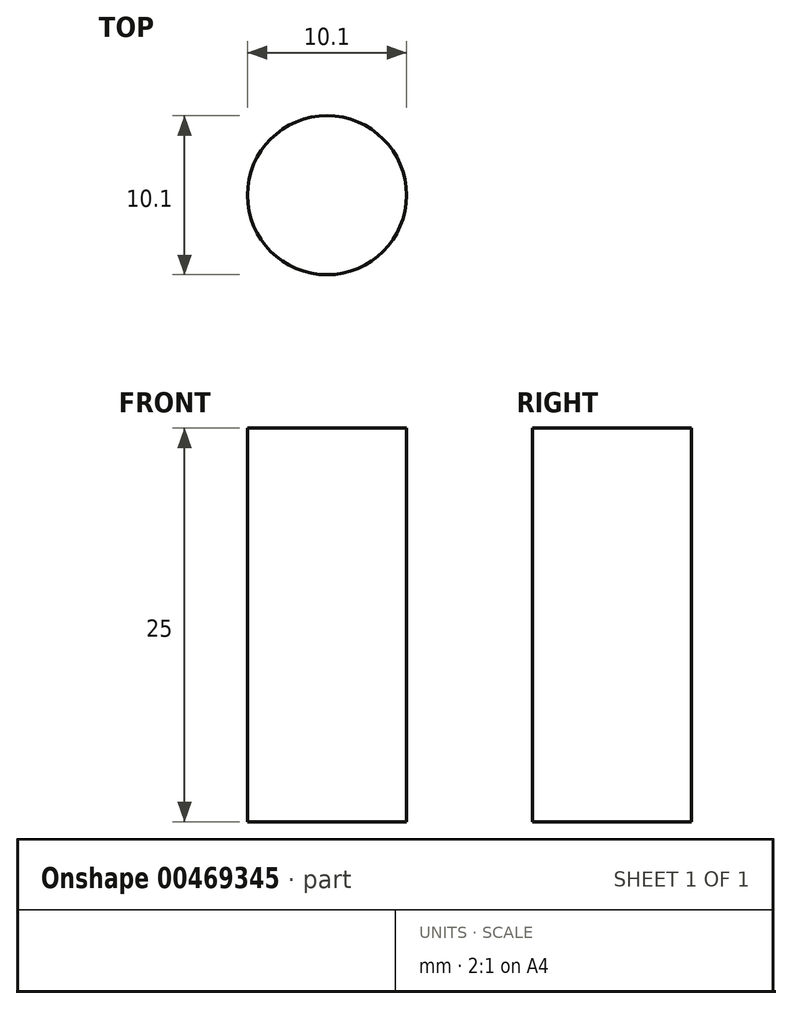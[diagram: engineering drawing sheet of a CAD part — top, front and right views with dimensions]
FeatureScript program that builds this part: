
annotation { "Feature Type Name" : "Feature", "Feature Type Description" : "" }
export const myFeature = defineFeature(function(context is Context, id is Id, definition is map)
    precondition{}
    {
        {
            var Q0;
            Q0=qCreatedBy(makeId("Top.planeOp"),FACE);
            var sketch = newSketch(context, id + "F0", { "sketchPlane" : qUnion([Q0])});
            skLineSegment(sketch, "E0.bottom", {"start": v(0, 0) * mm, "end": v(250, 0) * mm});
            skLineSegment(sketch, "E0.top", {"start": v(0, -80) * mm, "end": v(250, -80) * mm});
            skLineSegment(sketch, "E0.left", {"start": v(0, 0) * mm, "end": v(0, -80) * mm});
            skLineSegment(sketch, "E0.right", {"start": v(250, 0) * mm, "end": v(250, -80) * mm});
            skLineSegment(sketch, "E1.bottom", {"start": v(0, -35) * mm, "end": v(250, -35) * mm});
            skLineSegment(sketch, "E1.top", {"start": v(0, -45) * mm, "end": v(250, -45) * mm});
            skLineSegment(sketch, "E1.left", {"start": v(0, -35) * mm, "end": v(0, -45) * mm});
            skLineSegment(sketch, "E1.right", {"start": v(250, -35) * mm, "end": v(250, -45) * mm});
            skPoint(sketch, "E1.middle", {"position": v(125, -40) * mm});
            skPoint(sketch, "E1.middle.positionSnap0", {"position": v(0, -40) * mm});
            skPoint(sketch, "E1.middle.positionSnap1", {"position": v(125, 0) * mm});
            skPoint(sketch, "E1.centerSnap0", {"position": v(0, -40) * mm});
            skPoint(sketch, "E1.centerSnap1", {"position": v(125, 0) * mm});
            skLineSegment(sketch, "E2.0", {"start": v(-5, 5) * mm, "end": v(-5, -85) * mm});
            skLineSegment(sketch, "E2.1", {"start": v(-5, 5) * mm, "end": v(255, 5) * mm});
            skLineSegment(sketch, "E2.2", {"start": v(255, 5) * mm, "end": v(255, -85) * mm});
            skLineSegment(sketch, "E2.3", {"start": v(-5, -85) * mm, "end": v(255, -85) * mm});
            skLineSegment(sketch, "E3", {"start": v(0, -40) * mm, "end": v(250, -40) * mm});
            skSolve(sketch);
        }
        {
            var Q0;
            Q0=qCreatedBy(makeId("Top.planeOp"),FACE);
            var sketch = newSketch(context, id + "F1", { "sketchPlane" : qUnion([Q0])});
            skLineSegment(sketch, "E4.bottom", {"start": v(0, 0) * mm, "end": v(250, 0) * mm});
            skLineSegment(sketch, "E4.top", {"start": v(0, -140) * mm, "end": v(250, -140) * mm});
            skLineSegment(sketch, "E4.left", {"start": v(0, 0) * mm, "end": v(0, -140) * mm});
            skLineSegment(sketch, "E4.right", {"start": v(250, 0) * mm, "end": v(250, -140) * mm});
            skLineSegment(sketch, "E5.bottom", {"start": v(0, -64) * mm, "end": v(250, -64) * mm});
            skLineSegment(sketch, "E5.top", {"start": v(0, -76) * mm, "end": v(250, -76) * mm});
            skLineSegment(sketch, "E5.left", {"start": v(0, -64) * mm, "end": v(0, -76) * mm});
            skLineSegment(sketch, "E5.right", {"start": v(250, -64) * mm, "end": v(250, -76) * mm});
            skPoint(sketch, "E5.middle", {"position": v(125, -70) * mm});
            skPoint(sketch, "E5.middle.positionSnap0", {"position": v(0, -70) * mm});
            skPoint(sketch, "E5.middle.positionSnap1", {"position": v(125, 0) * mm});
            skPoint(sketch, "E5.centerSnap0", {"position": v(0, -70) * mm});
            skPoint(sketch, "E5.centerSnap1", {"position": v(125, 0) * mm});
            skLineSegment(sketch, "E6.0", {"start": v(-5, 5) * mm, "end": v(-5, -145) * mm});
            skLineSegment(sketch, "E6.1", {"start": v(-5, 5) * mm, "end": v(255, 5) * mm});
            skLineSegment(sketch, "E6.2", {"start": v(255, 5) * mm, "end": v(255, -145) * mm});
            skLineSegment(sketch, "E6.3", {"start": v(-5, -145) * mm, "end": v(255, -145) * mm});
            skLineSegment(sketch, "E7", {"start": v(250, -70) * mm, "end": v(0, -70) * mm});
            skSolve(sketch);
        }
        {
            var Q0;
            Q0=qCreatedBy(makeId("Top.planeOp"),FACE);
            var sketch = newSketch(context, id + "F2", { "sketchPlane" : qUnion([Q0])});
            skLineSegment(sketch, "E8.bottom", {"start": v(0, 0) * mm, "end": v(250, 0) * mm});
            skLineSegment(sketch, "E8.top", {"start": v(0, -225) * mm, "end": v(250, -225) * mm});
            skLineSegment(sketch, "E8.left", {"start": v(0, 0) * mm, "end": v(0, -225) * mm});
            skLineSegment(sketch, "E8.right", {"start": v(250, 0) * mm, "end": v(250, -225) * mm});
            skLineSegment(sketch, "E9.bottom", {"start": v(0, -64) * mm, "end": v(250, -64) * mm});
            skLineSegment(sketch, "E9.top", {"start": v(0, -161) * mm, "end": v(250, -161) * mm});
            skLineSegment(sketch, "E9.left", {"start": v(0, -64) * mm, "end": v(0, -161) * mm});
            skLineSegment(sketch, "E9.right", {"start": v(250, -64) * mm, "end": v(250, -161) * mm});
            skPoint(sketch, "E9.middle", {"position": v(125, -112.5) * mm});
            skPoint(sketch, "E9.middle.positionSnap0", {"position": v(125, 0) * mm});
            skPoint(sketch, "E9.middle.positionSnap1", {"position": v(0, -112.5) * mm});
            skPoint(sketch, "E9.centerSnap0", {"position": v(125, 0) * mm});
            skPoint(sketch, "E9.centerSnap1", {"position": v(0, -112.5) * mm});
            skLineSegment(sketch, "E10.0", {"start": v(-5, 5) * mm, "end": v(-5, -230) * mm});
            skLineSegment(sketch, "E10.1", {"start": v(-5, 5) * mm, "end": v(255, 5) * mm});
            skLineSegment(sketch, "E10.2", {"start": v(255, 5) * mm, "end": v(255, -230) * mm});
            skLineSegment(sketch, "E10.3", {"start": v(-5, -230) * mm, "end": v(255, -230) * mm});
            skLineSegment(sketch, "E11", {"start": v(0, -112.5) * mm, "end": v(250, -112.5) * mm});
            skSolve(sketch);
        }
        {
            var Q0;
            Q0=qCreatedBy(makeId("Top.planeOp"),FACE);
            var sketch = newSketch(context, id + "F3", { "sketchPlane" : qUnion([Q0])});
            skLineSegment(sketch, "E12.0", {"start": v(-20, 20) * mm, "end": v(-20, -245) * mm});
            skLineSegment(sketch, "E12.1", {"start": v(-20, 20) * mm, "end": v(270, 20) * mm});
            skLineSegment(sketch, "E12.2", {"start": v(270, 20) * mm, "end": v(270, -245) * mm});
            skLineSegment(sketch, "E12.3", {"start": v(-20, -245) * mm, "end": v(270, -245) * mm});
            skLineSegment(sketch, "E13.0", {"start": v(20, 20) * mm, "end": v(20, -245) * mm});
            skLineSegment(sketch, "E14", {"start": v(125, 20) * mm, "end": v(125, -245) * mm});
            skLineSegment(sketch, "E15.MirrorCS", {"start": v(230, 20) * mm, "end": v(230, -245) * mm});
            skCircle(sketch, "E16", {"center": v(20, 5) * mm, "radius": 5.05 * mm});
            skCircle(sketch, "E17", {"center": v(-5, -15) * mm, "radius": 5.05 * mm});
            skCircle(sketch, "E18.MirrorC", {"center": v(255, -15) * mm, "radius": 5.05 * mm});
            skCircle(sketch, "E19.MirrorC", {"center": v(230, 5) * mm, "radius": 5.05 * mm});
            skCircle(sketch, "E20.MirrorC", {"center": v(-5, -65) * mm, "radius": 5.05 * mm});
            skCircle(sketch, "E21.MirrorC", {"center": v(20, -85) * mm, "radius": 5.05 * mm});
            skCircle(sketch, "E22.MirrorC", {"center": v(230, -85) * mm, "radius": 5.05 * mm});
            skCircle(sketch, "E23.MirrorC", {"center": v(255, -65) * mm, "radius": 5.05 * mm});
            skCircle(sketch, "E24", {"center": v(-5.05, -40) * mm, "radius": 5.05 * mm});
            skCircle(sketch, "E25.MirrorC", {"center": v(255.05, -40) * mm, "radius": 5.05 * mm});
            skCircle(sketch, "E26.MirrorC", {"center": v(-5, -125) * mm, "radius": 5.05 * mm});
            skCircle(sketch, "E27.MirrorC", {"center": v(20, -145) * mm, "radius": 5.05 * mm});
            skCircle(sketch, "E28.MirrorC", {"center": v(230, -145) * mm, "radius": 5.05 * mm});
            skCircle(sketch, "E29.MirrorC", {"center": v(255, -125) * mm, "radius": 5.05 * mm});
            skCircle(sketch, "E30.MirrorC", {"center": v(-5, -210) * mm, "radius": 5.05 * mm});
            skCircle(sketch, "E31.MirrorC", {"center": v(20, -230) * mm, "radius": 5.05 * mm});
            skCircle(sketch, "E32.MirrorC", {"center": v(230, -230) * mm, "radius": 5.05 * mm});
            skCircle(sketch, "E33.MirrorC", {"center": v(255, -210) * mm, "radius": 5.05 * mm});
            skSolve(sketch);
        }
        {
            var Q0;
            {var subQ6=sQuery(id+"F3.wireOp",EDGE,"E14");Q0=makeQuery(id+"F3.imprint","IMPRINT",FACE,{"disambiguationData":[TD([[makeQuery(id+"F3.imprint","IMPRINT",EDGE,{"derivedFrom":subQ6}),-1.0]])]});}
            var Q1;
            {var subQ5=sQuery(id+"F3.wireOp",EDGE,"E12.2");Q1=makeQuery(id+"F3.imprint","IMPRINT",FACE,{"disambiguationData":[TD([[makeQuery(id+"F3.imprint","IMPRINT",EDGE,{"derivedFrom":subQ5}),-1.0]])]});}
            var Q2;
            {var subQ8=sQuery(id+"F3.wireOp",EDGE,"E14");Q2=makeQuery(id+"F3.imprint","IMPRINT",FACE,{"disambiguationData":[TD([[makeQuery(id+"F3.imprint","IMPRINT",EDGE,{"derivedFrom":subQ8}),1.0]])]});}
            var Q3;
            {var subQ5=sQuery(id+"F3.wireOp",EDGE,"E12.0");Q3=makeQuery(id+"F3.imprint","IMPRINT",FACE,{"disambiguationData":[TD([[makeQuery(id+"F3.imprint","IMPRINT",EDGE,{"derivedFrom":subQ5}),1.0]])]});}
            var Q4;
            {var subQ0=sQuery(id+"F3.wireOp",EDGE,"E28.MirrorC");var subQ1=sQuery(id+"F3.wireOp",EDGE,"E15.MirrorCS");var subQ2=makeQuery(id+"F3.imprint","INTERSECT",VERTEX,{"disambiguationData":[OD(0.0)],"derivedFrom":[subQ1,subQ0]});Q4=makeQuery(id+"F3.imprint","IMPRINT",FACE,{"disambiguationData":[TD([[makeQuery(id+"F3.imprint","IMPRINT",EDGE,{"disambiguationData":[TD([[subQ2,-1.0]])],"derivedFrom":subQ1}),1.0]])]});}
            var Q5;
            {var subQ0=sQuery(id+"F3.wireOp",EDGE,"E32.MirrorC");var subQ1=sQuery(id+"F3.wireOp",EDGE,"E15.MirrorCS");var subQ2=makeQuery(id+"F3.imprint","INTERSECT",VERTEX,{"disambiguationData":[OD(0.0)],"derivedFrom":[subQ1,subQ0]});Q5=makeQuery(id+"F3.imprint","IMPRINT",FACE,{"disambiguationData":[TD([[makeQuery(id+"F3.imprint","IMPRINT",EDGE,{"disambiguationData":[TD([[subQ2,-1.0]])],"derivedFrom":subQ1}),1.0]])]});}
            var Q6;
            {var subQ0=sQuery(id+"F3.wireOp",EDGE,"E31.MirrorC");var subQ1=sQuery(id+"F3.wireOp",EDGE,"E13.0");var subQ2=makeQuery(id+"F3.imprint","INTERSECT",VERTEX,{"disambiguationData":[OD(0.0)],"derivedFrom":[subQ1,subQ0]});Q6=makeQuery(id+"F3.imprint","IMPRINT",FACE,{"disambiguationData":[TD([[makeQuery(id+"F3.imprint","IMPRINT",EDGE,{"disambiguationData":[TD([[subQ2,-1.0]])],"derivedFrom":subQ1}),-1.0]])]});}
            var Q7;
            {var subQ0=sQuery(id+"F3.wireOp",EDGE,"E32.MirrorC");var subQ1=sQuery(id+"F3.wireOp",EDGE,"E15.MirrorCS");var subQ2=makeQuery(id+"F3.imprint","INTERSECT",VERTEX,{"disambiguationData":[OD(0.0)],"derivedFrom":[subQ1,subQ0]});Q7=makeQuery(id+"F3.imprint","IMPRINT",FACE,{"disambiguationData":[TD([[makeQuery(id+"F3.imprint","IMPRINT",EDGE,{"disambiguationData":[TD([[subQ2,-1.0]])],"derivedFrom":subQ1}),-1.0]])]});}
            var Q8;
            {var subQ0=sQuery(id+"F3.wireOp",EDGE,"E31.MirrorC");var subQ1=sQuery(id+"F3.wireOp",EDGE,"E13.0");var subQ2=makeQuery(id+"F3.imprint","INTERSECT",VERTEX,{"disambiguationData":[OD(0.0)],"derivedFrom":[subQ1,subQ0]});Q8=makeQuery(id+"F3.imprint","IMPRINT",FACE,{"disambiguationData":[TD([[makeQuery(id+"F3.imprint","IMPRINT",EDGE,{"disambiguationData":[TD([[subQ2,-1.0]])],"derivedFrom":subQ1}),1.0]])]});}
            var Q9;
            {var subQ0=sQuery(id+"F3.wireOp",EDGE,"E28.MirrorC");var subQ1=sQuery(id+"F3.wireOp",EDGE,"E15.MirrorCS");var subQ2=makeQuery(id+"F3.imprint","INTERSECT",VERTEX,{"disambiguationData":[OD(0.0)],"derivedFrom":[subQ1,subQ0]});Q9=makeQuery(id+"F3.imprint","IMPRINT",FACE,{"disambiguationData":[TD([[makeQuery(id+"F3.imprint","IMPRINT",EDGE,{"disambiguationData":[TD([[subQ2,-1.0]])],"derivedFrom":subQ1}),-1.0]])]});}
            var Q10;
            {var subQ0=sQuery(id+"F3.wireOp",EDGE,"E22.MirrorC");var subQ1=sQuery(id+"F3.wireOp",EDGE,"E15.MirrorCS");var subQ2=makeQuery(id+"F3.imprint","INTERSECT",VERTEX,{"disambiguationData":[OD(0.0)],"derivedFrom":[subQ1,subQ0]});Q10=makeQuery(id+"F3.imprint","IMPRINT",FACE,{"disambiguationData":[TD([[makeQuery(id+"F3.imprint","IMPRINT",EDGE,{"disambiguationData":[TD([[subQ2,-1.0]])],"derivedFrom":subQ1}),1.0]])]});}
            var Q11;
            {var subQ0=sQuery(id+"F3.wireOp",EDGE,"E27.MirrorC");var subQ1=sQuery(id+"F3.wireOp",EDGE,"E13.0");var subQ2=makeQuery(id+"F3.imprint","INTERSECT",VERTEX,{"disambiguationData":[OD(0.0)],"derivedFrom":[subQ1,subQ0]});Q11=makeQuery(id+"F3.imprint","IMPRINT",FACE,{"disambiguationData":[TD([[makeQuery(id+"F3.imprint","IMPRINT",EDGE,{"disambiguationData":[TD([[subQ2,-1.0]])],"derivedFrom":subQ1}),1.0]])]});}
            var Q12;
            Q12=makeQuery(id+"F3.imprint","IMPRINT",FACE,{"disambiguationData":[TD([[makeQuery(id+"F3.imprint","IMPRINT",EDGE,{"derivedFrom":sQuery(id+"F3.wireOp",EDGE,"E17")}),1.0]])]});
            var Q13;
            {var subQ0=sQuery(id+"F3.wireOp",EDGE,"E27.MirrorC");var subQ1=sQuery(id+"F3.wireOp",EDGE,"E13.0");var subQ2=makeQuery(id+"F3.imprint","INTERSECT",VERTEX,{"disambiguationData":[OD(0.0)],"derivedFrom":[subQ1,subQ0]});Q13=makeQuery(id+"F3.imprint","IMPRINT",FACE,{"disambiguationData":[TD([[makeQuery(id+"F3.imprint","IMPRINT",EDGE,{"disambiguationData":[TD([[subQ2,-1.0]])],"derivedFrom":subQ1}),-1.0]])]});}
            var Q14;
            {var subQ0=sQuery(id+"F3.wireOp",EDGE,"E21.MirrorC");var subQ1=sQuery(id+"F3.wireOp",EDGE,"E13.0");var subQ2=makeQuery(id+"F3.imprint","INTERSECT",VERTEX,{"disambiguationData":[OD(0.0)],"derivedFrom":[subQ1,subQ0]});Q14=makeQuery(id+"F3.imprint","IMPRINT",FACE,{"disambiguationData":[TD([[makeQuery(id+"F3.imprint","IMPRINT",EDGE,{"disambiguationData":[TD([[subQ2,-1.0]])],"derivedFrom":subQ1}),1.0]])]});}
            var Q15;
            Q15=makeQuery(id+"F3.imprint","IMPRINT",FACE,{"disambiguationData":[TD([[makeQuery(id+"F3.imprint","IMPRINT",EDGE,{"derivedFrom":sQuery(id+"F3.wireOp",EDGE,"E20.MirrorC")}),-1.0]])]});
            var Q16;
            Q16=makeQuery(id+"F3.imprint","IMPRINT",FACE,{"disambiguationData":[TD([[makeQuery(id+"F3.imprint","IMPRINT",EDGE,{"derivedFrom":sQuery(id+"F3.wireOp",EDGE,"E24")}),1.0]])]});
            var Q17;
            Q17=makeQuery(id+"F3.imprint","IMPRINT",FACE,{"disambiguationData":[TD([[makeQuery(id+"F3.imprint","IMPRINT",EDGE,{"derivedFrom":sQuery(id+"F3.wireOp",EDGE,"E25.MirrorC")}),-1.0]])]});
            var Q18;
            Q18=makeQuery(id+"F3.imprint","IMPRINT",FACE,{"disambiguationData":[TD([[makeQuery(id+"F3.imprint","IMPRINT",EDGE,{"derivedFrom":sQuery(id+"F3.wireOp",EDGE,"E29.MirrorC")}),1.0]])]});
            var Q19;
            Q19=makeQuery(id+"F3.imprint","IMPRINT",FACE,{"disambiguationData":[TD([[makeQuery(id+"F3.imprint","IMPRINT",EDGE,{"derivedFrom":sQuery(id+"F3.wireOp",EDGE,"E23.MirrorC")}),1.0]])]});
            var Q20;
            Q20=makeQuery(id+"F3.imprint","IMPRINT",FACE,{"disambiguationData":[TD([[makeQuery(id+"F3.imprint","IMPRINT",EDGE,{"derivedFrom":sQuery(id+"F3.wireOp",EDGE,"E26.MirrorC")}),-1.0]])]});
            var Q21;
            Q21=makeQuery(id+"F3.imprint","IMPRINT",FACE,{"disambiguationData":[TD([[makeQuery(id+"F3.imprint","IMPRINT",EDGE,{"derivedFrom":sQuery(id+"F3.wireOp",EDGE,"E30.MirrorC")}),-1.0]])]});
            var Q22;
            Q22=makeQuery(id+"F3.imprint","IMPRINT",FACE,{"disambiguationData":[TD([[makeQuery(id+"F3.imprint","IMPRINT",EDGE,{"derivedFrom":sQuery(id+"F3.wireOp",EDGE,"E33.MirrorC")}),1.0]])]});
            var Q23;
            {var subQ0=sQuery(id+"F3.wireOp",EDGE,"E16");var subQ1=sQuery(id+"F3.wireOp",EDGE,"E13.0");var subQ2=makeQuery(id+"F3.imprint","INTERSECT",VERTEX,{"disambiguationData":[OD(0.0)],"derivedFrom":[subQ1,subQ0]});Q23=makeQuery(id+"F3.imprint","IMPRINT",FACE,{"disambiguationData":[TD([[makeQuery(id+"F3.imprint","IMPRINT",EDGE,{"disambiguationData":[TD([[subQ2,-1.0]])],"derivedFrom":subQ1}),-1.0]])]});}
            var Q24;
            {var subQ0=sQuery(id+"F3.wireOp",EDGE,"E22.MirrorC");var subQ1=sQuery(id+"F3.wireOp",EDGE,"E15.MirrorCS");var subQ2=makeQuery(id+"F3.imprint","INTERSECT",VERTEX,{"disambiguationData":[OD(0.0)],"derivedFrom":[subQ1,subQ0]});Q24=makeQuery(id+"F3.imprint","IMPRINT",FACE,{"disambiguationData":[TD([[makeQuery(id+"F3.imprint","IMPRINT",EDGE,{"disambiguationData":[TD([[subQ2,-1.0]])],"derivedFrom":subQ1}),-1.0]])]});}
            var Q25;
            {var subQ0=sQuery(id+"F3.wireOp",EDGE,"E16");var subQ1=sQuery(id+"F3.wireOp",EDGE,"E13.0");var subQ2=makeQuery(id+"F3.imprint","INTERSECT",VERTEX,{"disambiguationData":[OD(0.0)],"derivedFrom":[subQ1,subQ0]});Q25=makeQuery(id+"F3.imprint","IMPRINT",FACE,{"disambiguationData":[TD([[makeQuery(id+"F3.imprint","IMPRINT",EDGE,{"disambiguationData":[TD([[subQ2,-1.0]])],"derivedFrom":subQ1}),1.0]])]});}
            var Q26;
            {var subQ0=sQuery(id+"F3.wireOp",EDGE,"E21.MirrorC");var subQ1=sQuery(id+"F3.wireOp",EDGE,"E13.0");var subQ2=makeQuery(id+"F3.imprint","INTERSECT",VERTEX,{"disambiguationData":[OD(0.0)],"derivedFrom":[subQ1,subQ0]});Q26=makeQuery(id+"F3.imprint","IMPRINT",FACE,{"disambiguationData":[TD([[makeQuery(id+"F3.imprint","IMPRINT",EDGE,{"disambiguationData":[TD([[subQ2,-1.0]])],"derivedFrom":subQ1}),-1.0]])]});}
            var Q27;
            {var subQ0=sQuery(id+"F3.wireOp",EDGE,"E19.MirrorC");var subQ1=sQuery(id+"F3.wireOp",EDGE,"E15.MirrorCS");var subQ2=makeQuery(id+"F3.imprint","INTERSECT",VERTEX,{"disambiguationData":[OD(0.0)],"derivedFrom":[subQ1,subQ0]});Q27=makeQuery(id+"F3.imprint","IMPRINT",FACE,{"disambiguationData":[TD([[makeQuery(id+"F3.imprint","IMPRINT",EDGE,{"disambiguationData":[TD([[subQ2,-1.0]])],"derivedFrom":subQ1}),1.0]])]});}
            var Q28;
            {var subQ0=sQuery(id+"F3.wireOp",EDGE,"E19.MirrorC");var subQ1=sQuery(id+"F3.wireOp",EDGE,"E15.MirrorCS");var subQ2=makeQuery(id+"F3.imprint","INTERSECT",VERTEX,{"disambiguationData":[OD(0.0)],"derivedFrom":[subQ1,subQ0]});Q28=makeQuery(id+"F3.imprint","IMPRINT",FACE,{"disambiguationData":[TD([[makeQuery(id+"F3.imprint","IMPRINT",EDGE,{"disambiguationData":[TD([[subQ2,-1.0]])],"derivedFrom":subQ1}),-1.0]])]});}
            var Q29;
            Q29=makeQuery(id+"F3.imprint","IMPRINT",FACE,{"disambiguationData":[TD([[makeQuery(id+"F3.imprint","IMPRINT",EDGE,{"derivedFrom":sQuery(id+"F3.wireOp",EDGE,"E18.MirrorC")}),-1.0]])]});
            extrude(context, id + "F4", {"entities" : qUnion([Q0, Q1, Q2, Q3, Q4, Q5, Q6, Q7, Q8, Q9, Q10, Q11, Q12, Q13, Q14, Q15, Q16, Q17, Q18, Q19, Q20, Q21, Q22, Q23, Q24, Q25, Q26, Q27, Q28, Q29]), "oppositeDirection" : true, "depth" : 25 * mm});
        }
        {
            var Q0;
            Q0=makeQuery(id+"F3.imprint","IMPRINT",FACE,{"disambiguationData":[TD([[makeQuery(id+"F3.imprint","IMPRINT",EDGE,{"derivedFrom":sQuery(id+"F3.wireOp",EDGE,"E17")}),1.0]])]});
            var Q1;
            {var subQ0=sQuery(id+"F3.wireOp",EDGE,"E16");var subQ1=sQuery(id+"F3.wireOp",EDGE,"E13.0");var subQ2=makeQuery(id+"F3.imprint","INTERSECT",VERTEX,{"disambiguationData":[OD(0.0)],"derivedFrom":[subQ1,subQ0]});Q1=makeQuery(id+"F3.imprint","IMPRINT",FACE,{"disambiguationData":[TD([[makeQuery(id+"F3.imprint","IMPRINT",EDGE,{"disambiguationData":[TD([[subQ2,-1.0]])],"derivedFrom":subQ1}),1.0]])]});}
            var Q2;
            {var subQ0=sQuery(id+"F3.wireOp",EDGE,"E16");var subQ1=sQuery(id+"F3.wireOp",EDGE,"E13.0");var subQ2=makeQuery(id+"F3.imprint","INTERSECT",VERTEX,{"disambiguationData":[OD(0.0)],"derivedFrom":[subQ1,subQ0]});Q2=makeQuery(id+"F3.imprint","IMPRINT",FACE,{"disambiguationData":[TD([[makeQuery(id+"F3.imprint","IMPRINT",EDGE,{"disambiguationData":[TD([[subQ2,-1.0]])],"derivedFrom":subQ1}),-1.0]])]});}
            var Q3;
            Q3=makeQuery(id+"F3.imprint","IMPRINT",FACE,{"disambiguationData":[TD([[makeQuery(id+"F3.imprint","IMPRINT",EDGE,{"derivedFrom":sQuery(id+"F3.wireOp",EDGE,"E20.MirrorC")}),-1.0]])]});
            var Q4;
            {var subQ0=sQuery(id+"F3.wireOp",EDGE,"E21.MirrorC");var subQ1=sQuery(id+"F3.wireOp",EDGE,"E13.0");var subQ2=makeQuery(id+"F3.imprint","INTERSECT",VERTEX,{"disambiguationData":[OD(0.0)],"derivedFrom":[subQ1,subQ0]});Q4=makeQuery(id+"F3.imprint","IMPRINT",FACE,{"disambiguationData":[TD([[makeQuery(id+"F3.imprint","IMPRINT",EDGE,{"disambiguationData":[TD([[subQ2,-1.0]])],"derivedFrom":subQ1}),1.0]])]});}
            var Q5;
            {var subQ0=sQuery(id+"F3.wireOp",EDGE,"E21.MirrorC");var subQ1=sQuery(id+"F3.wireOp",EDGE,"E13.0");var subQ2=makeQuery(id+"F3.imprint","INTERSECT",VERTEX,{"disambiguationData":[OD(0.0)],"derivedFrom":[subQ1,subQ0]});Q5=makeQuery(id+"F3.imprint","IMPRINT",FACE,{"disambiguationData":[TD([[makeQuery(id+"F3.imprint","IMPRINT",EDGE,{"disambiguationData":[TD([[subQ2,-1.0]])],"derivedFrom":subQ1}),-1.0]])]});}
            var Q6;
            Q6=makeQuery(id+"F3.imprint","IMPRINT",FACE,{"disambiguationData":[TD([[makeQuery(id+"F3.imprint","IMPRINT",EDGE,{"derivedFrom":sQuery(id+"F3.wireOp",EDGE,"E26.MirrorC")}),-1.0]])]});
            var Q7;
            {var subQ0=sQuery(id+"F3.wireOp",EDGE,"E27.MirrorC");var subQ1=sQuery(id+"F3.wireOp",EDGE,"E13.0");var subQ2=makeQuery(id+"F3.imprint","INTERSECT",VERTEX,{"disambiguationData":[OD(0.0)],"derivedFrom":[subQ1,subQ0]});Q7=makeQuery(id+"F3.imprint","IMPRINT",FACE,{"disambiguationData":[TD([[makeQuery(id+"F3.imprint","IMPRINT",EDGE,{"disambiguationData":[TD([[subQ2,-1.0]])],"derivedFrom":subQ1}),1.0]])]});}
            var Q8;
            {var subQ0=sQuery(id+"F3.wireOp",EDGE,"E27.MirrorC");var subQ1=sQuery(id+"F3.wireOp",EDGE,"E13.0");var subQ2=makeQuery(id+"F3.imprint","INTERSECT",VERTEX,{"disambiguationData":[OD(0.0)],"derivedFrom":[subQ1,subQ0]});Q8=makeQuery(id+"F3.imprint","IMPRINT",FACE,{"disambiguationData":[TD([[makeQuery(id+"F3.imprint","IMPRINT",EDGE,{"disambiguationData":[TD([[subQ2,-1.0]])],"derivedFrom":subQ1}),-1.0]])]});}
            var Q9;
            Q9=makeQuery(id+"F3.imprint","IMPRINT",FACE,{"disambiguationData":[TD([[makeQuery(id+"F3.imprint","IMPRINT",EDGE,{"derivedFrom":sQuery(id+"F3.wireOp",EDGE,"E30.MirrorC")}),-1.0]])]});
            var Q10;
            {var subQ0=sQuery(id+"F3.wireOp",EDGE,"E31.MirrorC");var subQ1=sQuery(id+"F3.wireOp",EDGE,"E13.0");var subQ2=makeQuery(id+"F3.imprint","INTERSECT",VERTEX,{"disambiguationData":[OD(0.0)],"derivedFrom":[subQ1,subQ0]});Q10=makeQuery(id+"F3.imprint","IMPRINT",FACE,{"disambiguationData":[TD([[makeQuery(id+"F3.imprint","IMPRINT",EDGE,{"disambiguationData":[TD([[subQ2,-1.0]])],"derivedFrom":subQ1}),-1.0]])]});}
            var Q11;
            {var subQ0=sQuery(id+"F3.wireOp",EDGE,"E31.MirrorC");var subQ1=sQuery(id+"F3.wireOp",EDGE,"E13.0");var subQ2=makeQuery(id+"F3.imprint","INTERSECT",VERTEX,{"disambiguationData":[OD(0.0)],"derivedFrom":[subQ1,subQ0]});Q11=makeQuery(id+"F3.imprint","IMPRINT",FACE,{"disambiguationData":[TD([[makeQuery(id+"F3.imprint","IMPRINT",EDGE,{"disambiguationData":[TD([[subQ2,-1.0]])],"derivedFrom":subQ1}),1.0]])]});}
            var Q12;
            {var subQ0=sQuery(id+"F3.wireOp",EDGE,"E32.MirrorC");var subQ1=sQuery(id+"F3.wireOp",EDGE,"E15.MirrorCS");var subQ2=makeQuery(id+"F3.imprint","INTERSECT",VERTEX,{"disambiguationData":[OD(0.0)],"derivedFrom":[subQ1,subQ0]});Q12=makeQuery(id+"F3.imprint","IMPRINT",FACE,{"disambiguationData":[TD([[makeQuery(id+"F3.imprint","IMPRINT",EDGE,{"disambiguationData":[TD([[subQ2,-1.0]])],"derivedFrom":subQ1}),-1.0]])]});}
            var Q13;
            {var subQ0=sQuery(id+"F3.wireOp",EDGE,"E32.MirrorC");var subQ1=sQuery(id+"F3.wireOp",EDGE,"E15.MirrorCS");var subQ2=makeQuery(id+"F3.imprint","INTERSECT",VERTEX,{"disambiguationData":[OD(0.0)],"derivedFrom":[subQ1,subQ0]});Q13=makeQuery(id+"F3.imprint","IMPRINT",FACE,{"disambiguationData":[TD([[makeQuery(id+"F3.imprint","IMPRINT",EDGE,{"disambiguationData":[TD([[subQ2,-1.0]])],"derivedFrom":subQ1}),1.0]])]});}
            var Q14;
            Q14=makeQuery(id+"F3.imprint","IMPRINT",FACE,{"disambiguationData":[TD([[makeQuery(id+"F3.imprint","IMPRINT",EDGE,{"derivedFrom":sQuery(id+"F3.wireOp",EDGE,"E33.MirrorC")}),1.0]])]});
            var Q15;
            {var subQ0=sQuery(id+"F3.wireOp",EDGE,"E28.MirrorC");var subQ1=sQuery(id+"F3.wireOp",EDGE,"E15.MirrorCS");var subQ2=makeQuery(id+"F3.imprint","INTERSECT",VERTEX,{"disambiguationData":[OD(0.0)],"derivedFrom":[subQ1,subQ0]});Q15=makeQuery(id+"F3.imprint","IMPRINT",FACE,{"disambiguationData":[TD([[makeQuery(id+"F3.imprint","IMPRINT",EDGE,{"disambiguationData":[TD([[subQ2,-1.0]])],"derivedFrom":subQ1}),1.0]])]});}
            var Q16;
            {var subQ0=sQuery(id+"F3.wireOp",EDGE,"E28.MirrorC");var subQ1=sQuery(id+"F3.wireOp",EDGE,"E15.MirrorCS");var subQ2=makeQuery(id+"F3.imprint","INTERSECT",VERTEX,{"disambiguationData":[OD(0.0)],"derivedFrom":[subQ1,subQ0]});Q16=makeQuery(id+"F3.imprint","IMPRINT",FACE,{"disambiguationData":[TD([[makeQuery(id+"F3.imprint","IMPRINT",EDGE,{"disambiguationData":[TD([[subQ2,-1.0]])],"derivedFrom":subQ1}),-1.0]])]});}
            var Q17;
            Q17=makeQuery(id+"F3.imprint","IMPRINT",FACE,{"disambiguationData":[TD([[makeQuery(id+"F3.imprint","IMPRINT",EDGE,{"derivedFrom":sQuery(id+"F3.wireOp",EDGE,"E29.MirrorC")}),1.0]])]});
            var Q18;
            {var subQ0=sQuery(id+"F3.wireOp",EDGE,"E22.MirrorC");var subQ1=sQuery(id+"F3.wireOp",EDGE,"E15.MirrorCS");var subQ2=makeQuery(id+"F3.imprint","INTERSECT",VERTEX,{"disambiguationData":[OD(0.0)],"derivedFrom":[subQ1,subQ0]});Q18=makeQuery(id+"F3.imprint","IMPRINT",FACE,{"disambiguationData":[TD([[makeQuery(id+"F3.imprint","IMPRINT",EDGE,{"disambiguationData":[TD([[subQ2,-1.0]])],"derivedFrom":subQ1}),-1.0]])]});}
            var Q19;
            {var subQ0=sQuery(id+"F3.wireOp",EDGE,"E22.MirrorC");var subQ1=sQuery(id+"F3.wireOp",EDGE,"E15.MirrorCS");var subQ2=makeQuery(id+"F3.imprint","INTERSECT",VERTEX,{"disambiguationData":[OD(0.0)],"derivedFrom":[subQ1,subQ0]});Q19=makeQuery(id+"F3.imprint","IMPRINT",FACE,{"disambiguationData":[TD([[makeQuery(id+"F3.imprint","IMPRINT",EDGE,{"disambiguationData":[TD([[subQ2,-1.0]])],"derivedFrom":subQ1}),1.0]])]});}
            var Q20;
            Q20=makeQuery(id+"F3.imprint","IMPRINT",FACE,{"disambiguationData":[TD([[makeQuery(id+"F3.imprint","IMPRINT",EDGE,{"derivedFrom":sQuery(id+"F3.wireOp",EDGE,"E23.MirrorC")}),1.0]])]});
            var Q21;
            {var subQ0=sQuery(id+"F3.wireOp",EDGE,"E19.MirrorC");var subQ1=sQuery(id+"F3.wireOp",EDGE,"E15.MirrorCS");var subQ2=makeQuery(id+"F3.imprint","INTERSECT",VERTEX,{"disambiguationData":[OD(0.0)],"derivedFrom":[subQ1,subQ0]});Q21=makeQuery(id+"F3.imprint","IMPRINT",FACE,{"disambiguationData":[TD([[makeQuery(id+"F3.imprint","IMPRINT",EDGE,{"disambiguationData":[TD([[subQ2,-1.0]])],"derivedFrom":subQ1}),1.0]])]});}
            var Q22;
            {var subQ0=sQuery(id+"F3.wireOp",EDGE,"E19.MirrorC");var subQ1=sQuery(id+"F3.wireOp",EDGE,"E15.MirrorCS");var subQ2=makeQuery(id+"F3.imprint","INTERSECT",VERTEX,{"disambiguationData":[OD(0.0)],"derivedFrom":[subQ1,subQ0]});Q22=makeQuery(id+"F3.imprint","IMPRINT",FACE,{"disambiguationData":[TD([[makeQuery(id+"F3.imprint","IMPRINT",EDGE,{"disambiguationData":[TD([[subQ2,-1.0]])],"derivedFrom":subQ1}),-1.0]])]});}
            var Q23;
            Q23=makeQuery(id+"F3.imprint","IMPRINT",FACE,{"disambiguationData":[TD([[makeQuery(id+"F3.imprint","IMPRINT",EDGE,{"derivedFrom":sQuery(id+"F3.wireOp",EDGE,"E18.MirrorC")}),-1.0]])]});
            extrude(context, id + "F5", {"entities" : qUnion([Q0, Q1, Q2, Q3, Q4, Q5, Q6, Q7, Q8, Q9, Q10, Q11, Q12, Q13, Q14, Q15, Q16, Q17, Q18, Q19, Q20, Q21, Q22, Q23]), "operationType" : NewBodyOperationType.REMOVE, "oppositeDirection" : true, "depth" : 25 * mm});
        }
    });
